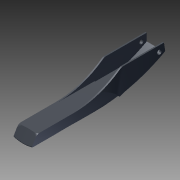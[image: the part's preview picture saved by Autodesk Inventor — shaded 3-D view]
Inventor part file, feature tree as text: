
AUTODESK INVENTOR PART (.ipt)
format: ipt  version: 2011 (Build 150239000, 239)  size: 451,072 bytes
history: native  units: mm (DEFAULTED — no unit token found)
features: other x5, plane x4, extrude x3, sketch x2, imported_body x1
ambient origin geometry x8: Origin, YZ Plane, XZ Plane, XY Plane, X Axis, Y Axis, Z Axis, Center Point
bodies: Solid1 (feature_tree)
feature tree (15):
  other  "Bottom - Master.ipt"
  extrude  "Extrusion1"  Depth=38.1mm
  plane  "Work Plane1"
  plane  "Work Plane2"
  plane  "Work Plane3"
  plane  "Work Plane4"
  other  "Side Cut"
  extrude  "Extrusion2"  Depth=114.3mm
  extrude  "Extrusion8"  Depth=25.4mm TaperAngle=0.0deg
  other  "Split Line"
  other  "Hinge"
  sketch  "Sketch3"  dims[d1=10.0mm d4=38.1mm]
  other  "Srf1"
  sketch  "Sketch7"  dims[d6=1.524mm d7=0.0mm d14=114.3mm d16=25.4mm d17=0.0mm d40=96.1136mm d42=-34.925mm d43=34.925mm d46=38.1mm d47=25.4mm d48=0.0mm]
  imported_body  "DerivedBody::Bottom - Master.ipt"
